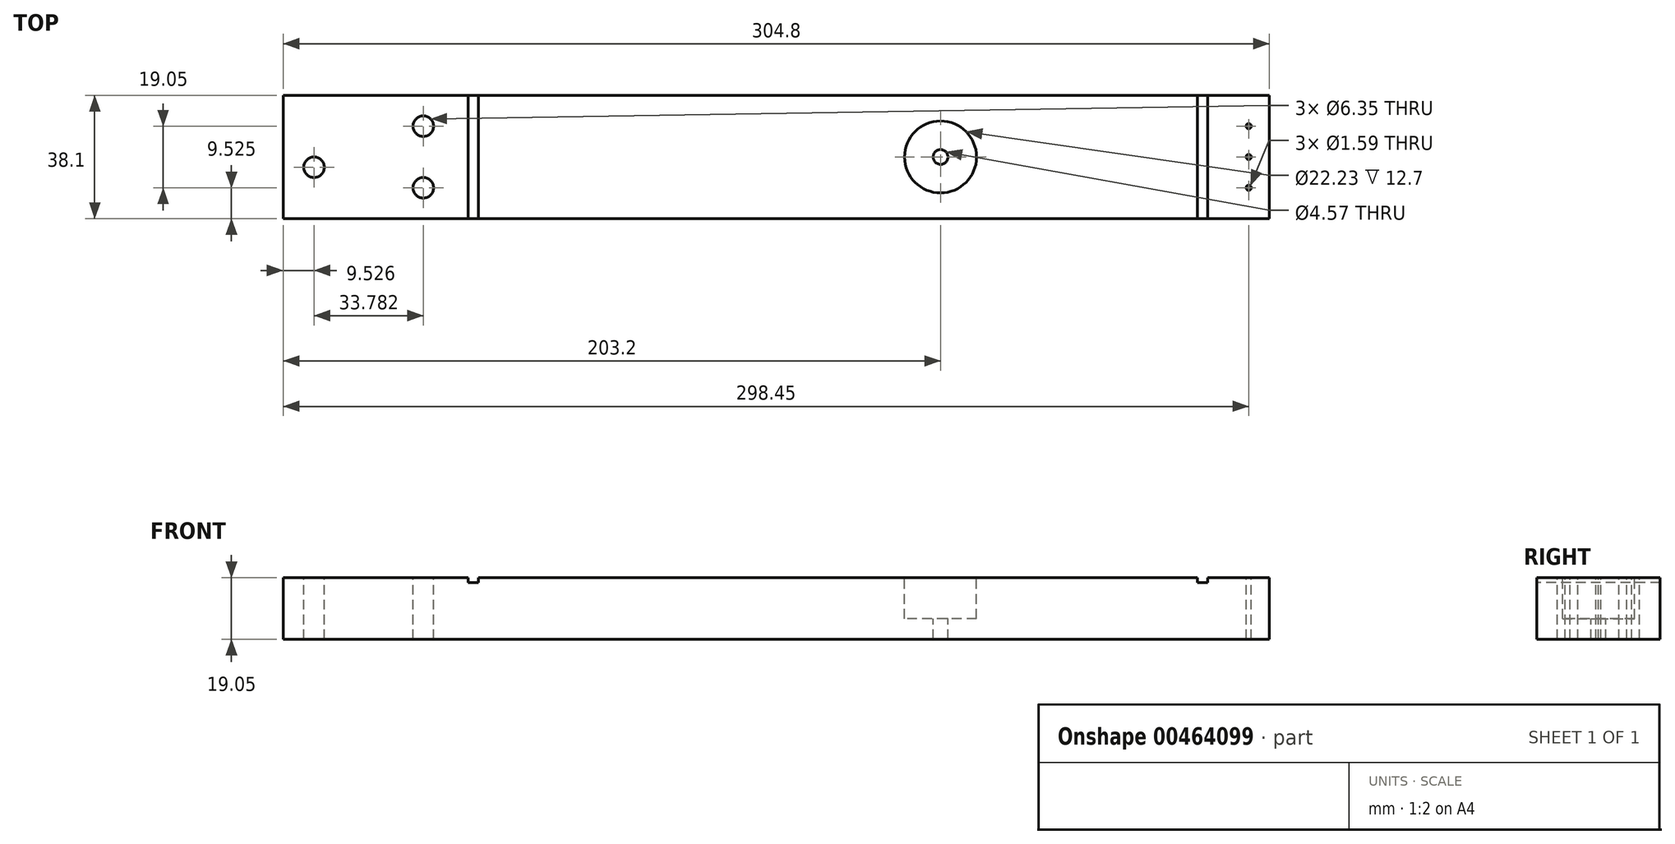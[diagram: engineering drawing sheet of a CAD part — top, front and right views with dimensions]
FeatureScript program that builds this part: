
annotation { "Feature Type Name" : "Feature", "Feature Type Description" : "" }
export const myFeature = defineFeature(function(context is Context, id is Id, definition is map)
    precondition{}
    {
        {
            var Q0;
            Q0=qCreatedBy(makeId("Top.planeOp"),FACE);
            var sketch = newSketch(context, id + "F0", { "sketchPlane" : qUnion([Q0])});
            skLineSegment(sketch, "E0.bottom", {"start": v(-67.92, 19.05) * mm, "end": v(236.88, 19.05) * mm});
            skLineSegment(sketch, "E0.top", {"start": v(-67.92, -19.05) * mm, "end": v(236.88, -19.05) * mm});
            skLineSegment(sketch, "E0.left", {"start": v(-67.92, 19.05) * mm, "end": v(-67.92, -19.05) * mm});
            skLineSegment(sketch, "E0.right", {"start": v(236.88, 19.05) * mm, "end": v(236.88, -19.05) * mm});
            skSolve(sketch);
        }
        {
            var Q0;
            Q0=qSketchRegion(id+"F0",true);
            extrude(context, id + "F1", {"entities" : qUnion([Q0]), "depth" : 19.05 * mm});
        }
        {
            var Q0;
            Q0=makeQuery(id+"F1.opExtrude","CAP_FACE",FACE,{"disambiguationData":[OSD([sQuery(id+"F0.wireOp",EDGE,"E0.bottom"),sQuery(id+"F0.wireOp",EDGE,"E0.top"),sQuery(id+"F0.wireOp",EDGE,"E0.left"),sQuery(id+"F0.wireOp",EDGE,"E0.right")])],"isStart":false});
            var sketch = newSketch(context, id + "F2", { "sketchPlane" : qUnion([Q0])});
            skCircle(sketch, "E1", {"center": v(135.28, 0) * mm, "radius": 11.11 * mm});
            skSolve(sketch);
        }
        {
            var Q0;
            Q0=qSketchRegion(id+"F2",true);
            extrude(context, id + "F3", {"entities" : qUnion([Q0]), "operationType" : NewBodyOperationType.REMOVE, "oppositeDirection" : true, "depth" : 12.7 * mm});
        }
        {
            var Q0;
            Q0=makeQuery(id+"F1.opExtrude","CAP_FACE",FACE,{"disambiguationData":[OSD([sQuery(id+"F0.wireOp",EDGE,"E0.bottom"),sQuery(id+"F0.wireOp",EDGE,"E0.top"),sQuery(id+"F0.wireOp",EDGE,"E0.left"),sQuery(id+"F0.wireOp",EDGE,"E0.right")])],"isStart":false});
            var sketch = newSketch(context, id + "F4", { "sketchPlane" : qUnion([Q0])});
            skCircle(sketch, "E2", {"center": v(-58.4, -3.18) * mm, "radius": 3.18 * mm});
            skPoint(sketch, "E3", {"position": v(-58.4, 0) * mm});
            skLineSegment(sketch, "E4", {"start": v(-58.4, 0) * mm, "end": v(135.28, 0) * mm, "construction": true});
            skSolve(sketch);
        }
        {
            var Q0;
            Q0=qSketchRegion(id+"F4",true);
            extrude(context, id + "F5", {"entities" : qUnion([Q0]), "operationType" : NewBodyOperationType.REMOVE, "endBound" : BoundingType.THROUGH_ALL, "oppositeDirection" : true, "depth" : 25.4 * mm});
        }
        {
            var Q0;
            Q0=makeQuery(id+"F1.opExtrude","CAP_FACE",FACE,{"disambiguationData":[OSD([sQuery(id+"F0.wireOp",EDGE,"E0.bottom"),sQuery(id+"F0.wireOp",EDGE,"E0.top"),sQuery(id+"F0.wireOp",EDGE,"E0.left"),sQuery(id+"F0.wireOp",EDGE,"E0.right")])],"isStart":false});
            var sketch = newSketch(context, id + "F6", { "sketchPlane" : qUnion([Q0])});
            skCircle(sketch, "E5", {"center": v(-24.61, -9.52) * mm, "radius": 3.18 * mm});
            skCircle(sketch, "E6", {"center": v(-24.61, 9.52) * mm, "radius": 3.18 * mm});
            skLineSegment(sketch, "E7", {"start": v(-61.89, 0) * mm, "end": v(-52.24, 0) * mm, "construction": true});
            skLineSegment(sketch, "E8", {"start": v(-28.72, 9.53) * mm, "end": v(-21.71, 9.53) * mm, "construction": true});
            skLineSegment(sketch, "E9", {"start": v(-29.2, -9.53) * mm, "end": v(-21.18, -9.53) * mm, "construction": true});
            skSolve(sketch);
        }
        {
            var Q0;
            Q0=qSketchRegion(id+"F6",true);
            extrude(context, id + "F7", {"entities" : qUnion([Q0]), "operationType" : NewBodyOperationType.REMOVE, "endBound" : BoundingType.THROUGH_ALL, "oppositeDirection" : true, "depth" : 25.4 * mm});
        }
        {
            var Q0;
            Q0=makeQuery(id+"F1.opExtrude","CAP_FACE",FACE,{"disambiguationData":[OSD([sQuery(id+"F0.wireOp",EDGE,"E0.bottom"),sQuery(id+"F0.wireOp",EDGE,"E0.top"),sQuery(id+"F0.wireOp",EDGE,"E0.left"),sQuery(id+"F0.wireOp",EDGE,"E0.right")])],"isStart":false});
            var sketch = newSketch(context, id + "F8", { "sketchPlane" : qUnion([Q0])});
            skLineSegment(sketch, "E10", {"start": v(230.53, 9.52) * mm, "end": v(230.53, -9.52) * mm, "construction": true});
            skCircle(sketch, "E11", {"center": v(230.53, 9.52) * mm, "radius": 0.8 * mm});
            skCircle(sketch, "E12", {"center": v(230.53, 0) * mm, "radius": 0.8 * mm});
            skCircle(sketch, "E13", {"center": v(230.53, -9.52) * mm, "radius": 0.8 * mm});
            skLineSegment(sketch, "E14", {"start": v(230.53, 0) * mm, "end": v(135.28, 0) * mm, "construction": true});
            skSolve(sketch);
        }
        {
            var Q0;
            Q0=qSketchRegion(id+"F8",true);
            extrude(context, id + "F9", {"entities" : qUnion([Q0]), "operationType" : NewBodyOperationType.REMOVE, "endBound" : BoundingType.THROUGH_ALL, "oppositeDirection" : true, "depth" : 25.4 * mm});
        }
        {
            var Q0;
            Q0=makeQuery(id+"F1.opExtrude","SWEPT_FACE",FACE,{"disambiguationData":[OSD([sQuery(id+"F0.wireOp",EDGE,"E0.top")])]});
            var sketch = newSketch(context, id + "F10", { "sketchPlane" : qUnion([Q0])});
            skLineSegment(sketch, "E15.bottom", {"start": v(-10.77, 19.05) * mm, "end": v(-7.6, 19.05) * mm});
            skLineSegment(sketch, "E15.top", {"start": v(-10.77, 17.46) * mm, "end": v(-7.6, 17.46) * mm});
            skLineSegment(sketch, "E15.left", {"start": v(-10.77, 19.05) * mm, "end": v(-10.77, 17.46) * mm});
            skLineSegment(sketch, "E15.right", {"start": v(-7.6, 19.05) * mm, "end": v(-7.6, 17.46) * mm});
            skLineSegment(sketch, "E16.bottom", {"start": v(214.66, 19.05) * mm, "end": v(217.83, 19.05) * mm});
            skLineSegment(sketch, "E16.top", {"start": v(214.66, 17.46) * mm, "end": v(217.83, 17.46) * mm});
            skLineSegment(sketch, "E16.left", {"start": v(214.66, 19.05) * mm, "end": v(214.66, 17.46) * mm});
            skLineSegment(sketch, "E16.right", {"start": v(217.83, 19.05) * mm, "end": v(217.83, 17.46) * mm});
            skSolve(sketch);
        }
        {
            var Q0;
            Q0=qSketchRegion(id+"F10",true);
            extrude(context, id + "F11", {"entities" : qUnion([Q0]), "operationType" : NewBodyOperationType.REMOVE, "endBound" : BoundingType.THROUGH_ALL, "oppositeDirection" : true, "depth" : 25.4 * mm});
        }
        {
            var Q0;
            Q0=makeQuery(id+"F3.boolean.opBoolean","COPY",FACE,{"derivedFrom":makeQuery(id+"F3.opExtrude","CAP_FACE",FACE,{"disambiguationData":[OSD([sQuery(id+"F2.wireOp",EDGE,"E1")])],"isStart":false})});
            var sketch = newSketch(context, id + "F12", { "sketchPlane" : qUnion([Q0])});
            skCircle(sketch, "E17", {"center": v(135.28, 0) * mm, "radius": 2.29 * mm});
            skSolve(sketch);
        }
        {
            var Q0;
            Q0=makeQuery(id+"F12.imprint","IMPRINT",FACE,{"disambiguationData":[TD([[makeQuery(id+"F12.imprint","IMPRINT",EDGE,{"derivedFrom":sQuery(id+"F12.wireOp",EDGE,"E17")}),1.0]])]});
            extrude(context, id + "F13", {"entities" : qUnion([Q0]), "operationType" : NewBodyOperationType.REMOVE, "endBound" : BoundingType.UP_TO_NEXT, "oppositeDirection" : true, "depth" : 25.4 * mm});
        }
    });
